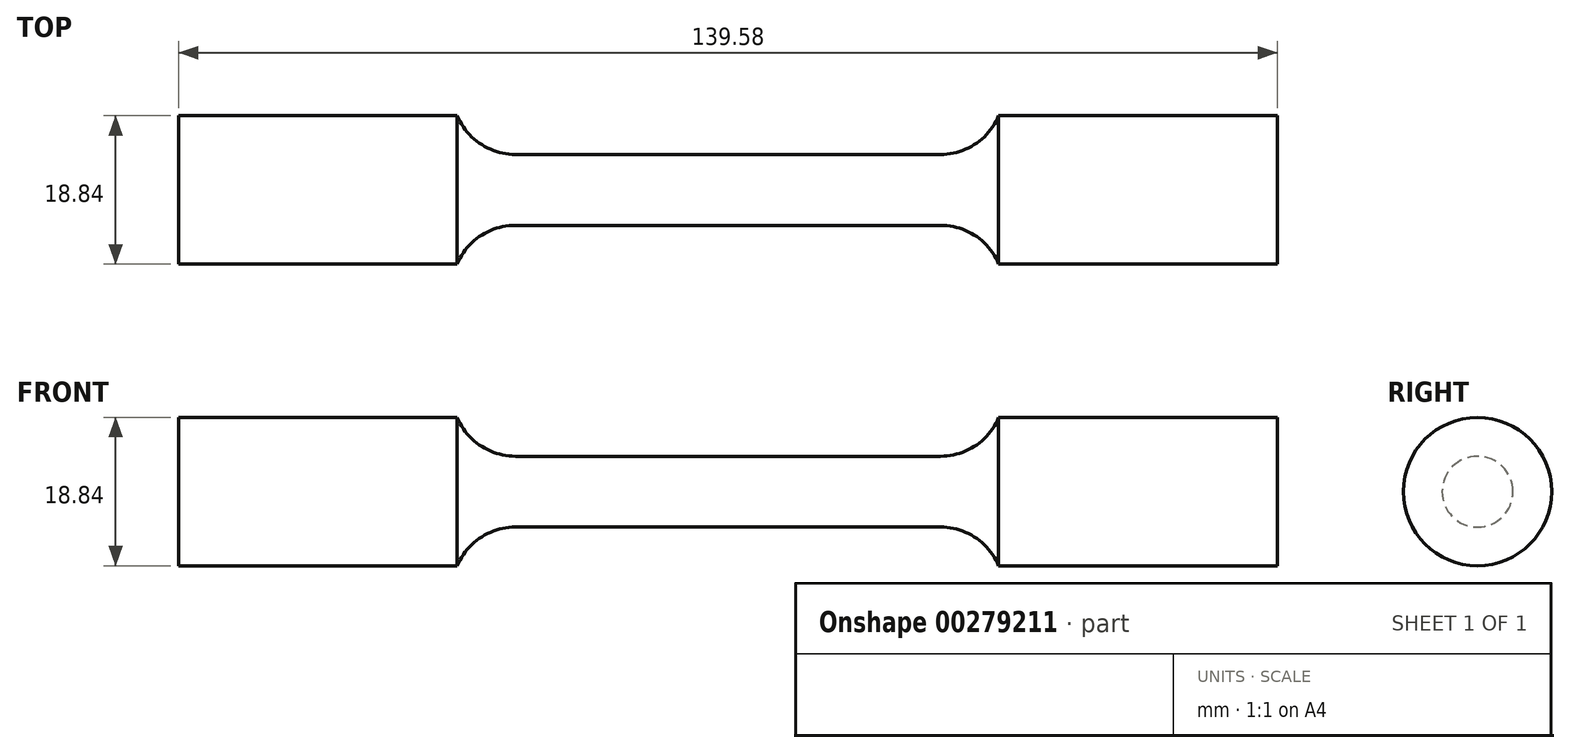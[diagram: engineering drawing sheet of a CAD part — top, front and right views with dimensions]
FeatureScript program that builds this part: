
annotation { "Feature Type Name" : "Feature", "Feature Type Description" : "" }
export const myFeature = defineFeature(function(context is Context, id is Id, definition is map)
    precondition{}
    {
        {
            var Q0;
            Q0=qCreatedBy(makeId("Front.planeOp"),FACE);
            var sketch = newSketch(context, id + "F0", { "sketchPlane" : qUnion([Q0])});
            skLineSegment(sketch, "E0", {"start": v(0, 4.5) * mm, "end": v(27, 4.5) * mm});
            skArc(sketch, "E1", {"start": v(27, 4.5) * mm, "mid": v(31.44, 5.84) * mm, "end": v(34.38, 9.42) * mm});
            skLineSegment(sketch, "E2", {"start": v(34.38, 9.42) * mm, "end": v(69.8, 9.42) * mm});
            skLineSegment(sketch, "E3", {"start": v(69.8, 9.42) * mm, "end": v(69.8, 0) * mm});
            skLineSegment(sketch, "E4.MirrorCS", {"start": v(0, 4.5) * mm, "end": v(-27, 4.5) * mm});
            skLineSegment(sketch, "E5.MirrorCS", {"start": v(-69.8, 9.42) * mm, "end": v(-69.8, 0) * mm});
            skLineSegment(sketch, "E6.MirrorCS", {"start": v(-34.38, 9.42) * mm, "end": v(-69.8, 9.42) * mm});
            skArc(sketch, "E7.MirrorCS", {"start": v(-27, 4.5) * mm, "mid": v(-31.44, 5.84) * mm, "end": v(-34.38, 9.42) * mm});
            skLineSegment(sketch, "E8", {"start": v(-69.8, 0) * mm, "end": v(69.8, 0) * mm});
            skSolve(sketch);
        }
        {
            var Q0;
            Q0 = qSketchRegion(id + "F0", true);
            var Q1;
            Q1=sQuery(id+"F0.wireOp",EDGE,"E8");
            revolve(context, id + "F1", {"entities" : qUnion([Q0]), "axis" : qUnion([Q1]), "revolveType" : RevolveType.FULL});
        }
    });
